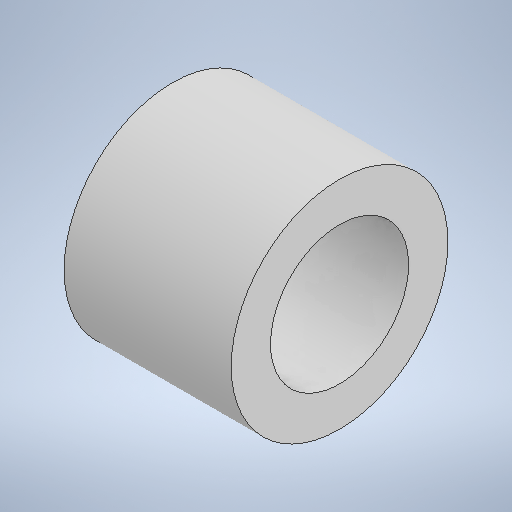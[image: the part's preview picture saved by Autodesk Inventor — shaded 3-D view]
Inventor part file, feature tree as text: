
AUTODESK INVENTOR PART (.ipt)
format: ipt  version: 2025.1 (Build 291241020, 241B)  size: 218,624 bytes
history: native  units: in
note: dims shown in document units (in); Inventor stores cm internally (conversion verified against a paired STEP export)
features: extrude x1, sketch x1
ambient origin geometry x8: Origin, YZ Plane, XZ Plane, XY Plane, X Axis, Y Axis, Z Axis, Center Point
bodies: Solid1 (feature_tree)
feature tree (2):
  extrude  "Extrusion1"  Depth=0.6174in
  sketch  "Sketch1"  dims[d0=0.51in d1=0.8in d2=0.6174in d3=0.0in]
